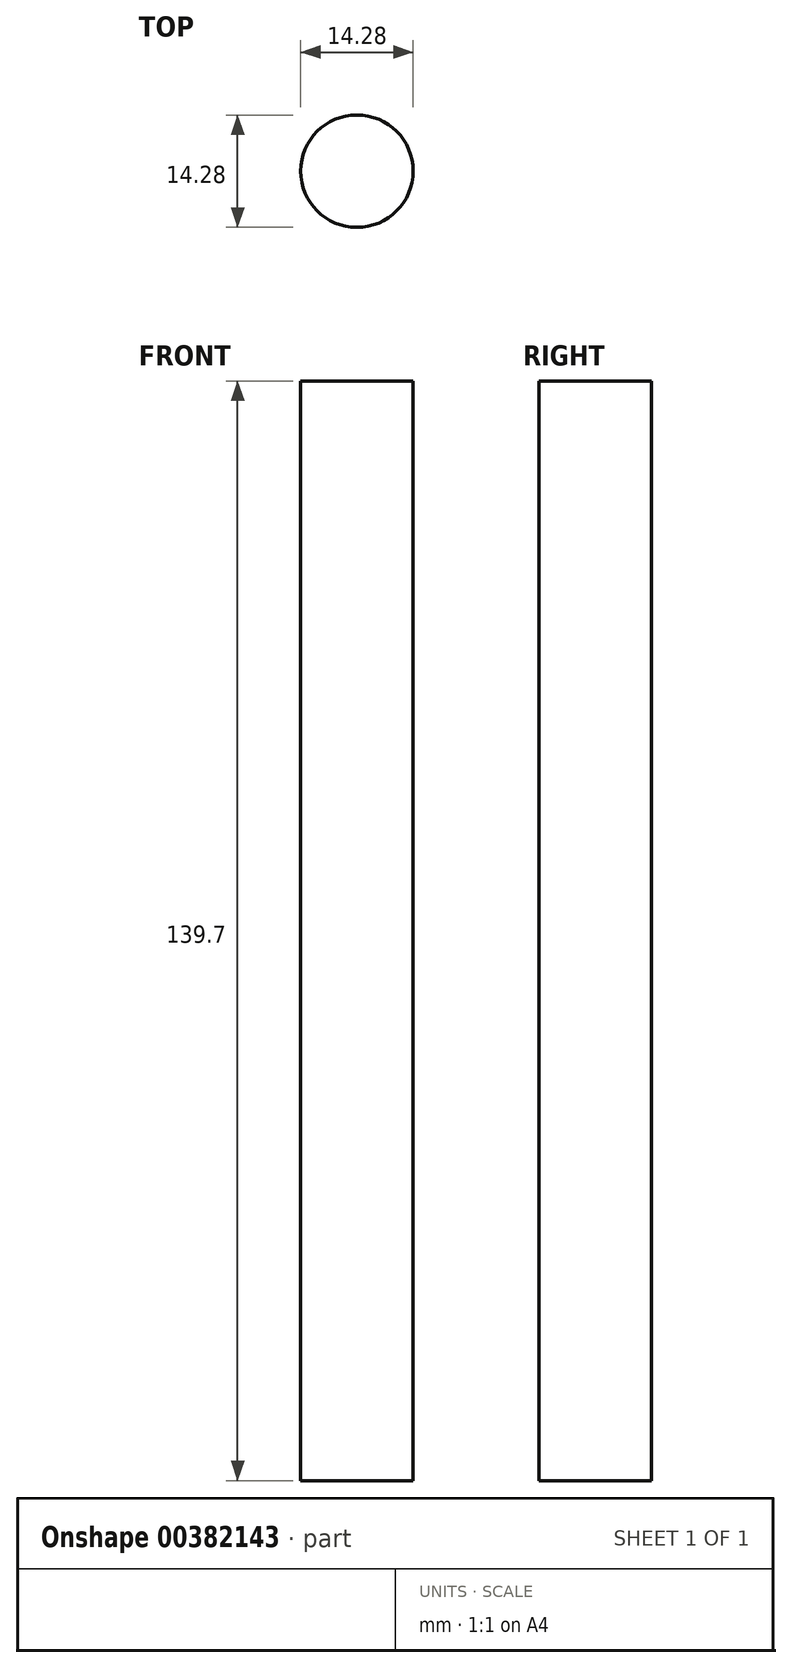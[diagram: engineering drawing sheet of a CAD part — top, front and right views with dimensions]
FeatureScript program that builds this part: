
annotation { "Feature Type Name" : "Feature", "Feature Type Description" : "" }
export const myFeature = defineFeature(function(context is Context, id is Id, definition is map)
    precondition{}
    {
        {
            var Q0;
            Q0=qCreatedBy(makeId("Top.planeOp"),FACE);
            var sketch = newSketch(context, id + "F0", { "sketchPlane" : qUnion([Q0])});
            skCircle(sketch, "E0", {"center": v(0, 0) * mm, "radius": 7.14 * mm});
            skSolve(sketch);
        }
        {
            var Q0;
            Q0=makeQuery(id+"F0.imprint","IMPRINT",FACE,{"disambiguationData":[TD([[makeQuery(id+"F0.imprint","IMPRINT",EDGE,{"derivedFrom":sQuery(id+"F0.wireOp",EDGE,"E0")}),1.0]])]});
            extrude(context, id + "F1", {"entities" : qUnion([Q0]), "depth" : 139.7 * mm});
        }
    });
